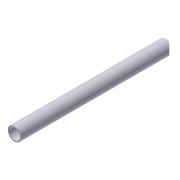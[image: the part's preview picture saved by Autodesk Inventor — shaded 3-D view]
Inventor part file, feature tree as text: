
AUTODESK INVENTOR PART (.ipt)
format: ipt  version: 2012 (Build 160160000, 160)  size: 95,232 bytes
history: native  units: in
note: dims shown in document units (in); Inventor stores cm internally (conversion verified against a paired STEP export)
features: extrude x3, sketch x3, projected_geometry x3, plane x1, other x1
ambient origin geometry x8: Origin, YZ Plane, XZ Plane, XY Plane, X Axis, Y Axis, Z Axis, Center Point
bodies: Solid1 (feature_tree)
feature tree (11):
  extrude  "Extrusion1"  Depth=1.375in
  plane  "Work Plane1"
  extrude  "Extrusion2"  TaperAngle=0.0deg  [1 undecoded]
  extrude  "Extrusion3"  Depth=1.6875in
  sketch  "Sketch1"  dims[d0=1.656in d1=1.375in]
  other  "Work Axis1"
  sketch  "Sketch2"  dims[d2=18.469in d3=0.0in d4=0.0in]
  projected_geometry  "Projected Loop1"
  projected_geometry  "Projected Loop2"
  sketch  "Sketch3"  dims[d5=18.9062in d6=1.6875in d7=11.875in d8=0.0in d9=0.25in d10=11.875in d11=0.0in]
  projected_geometry  "Projected Loop3"
note: 1 required parameter value undecoded (feature->parameter linkage not recoverable at this tier; creation-order binding heuristic only, values carry confidence <= 0.55)
